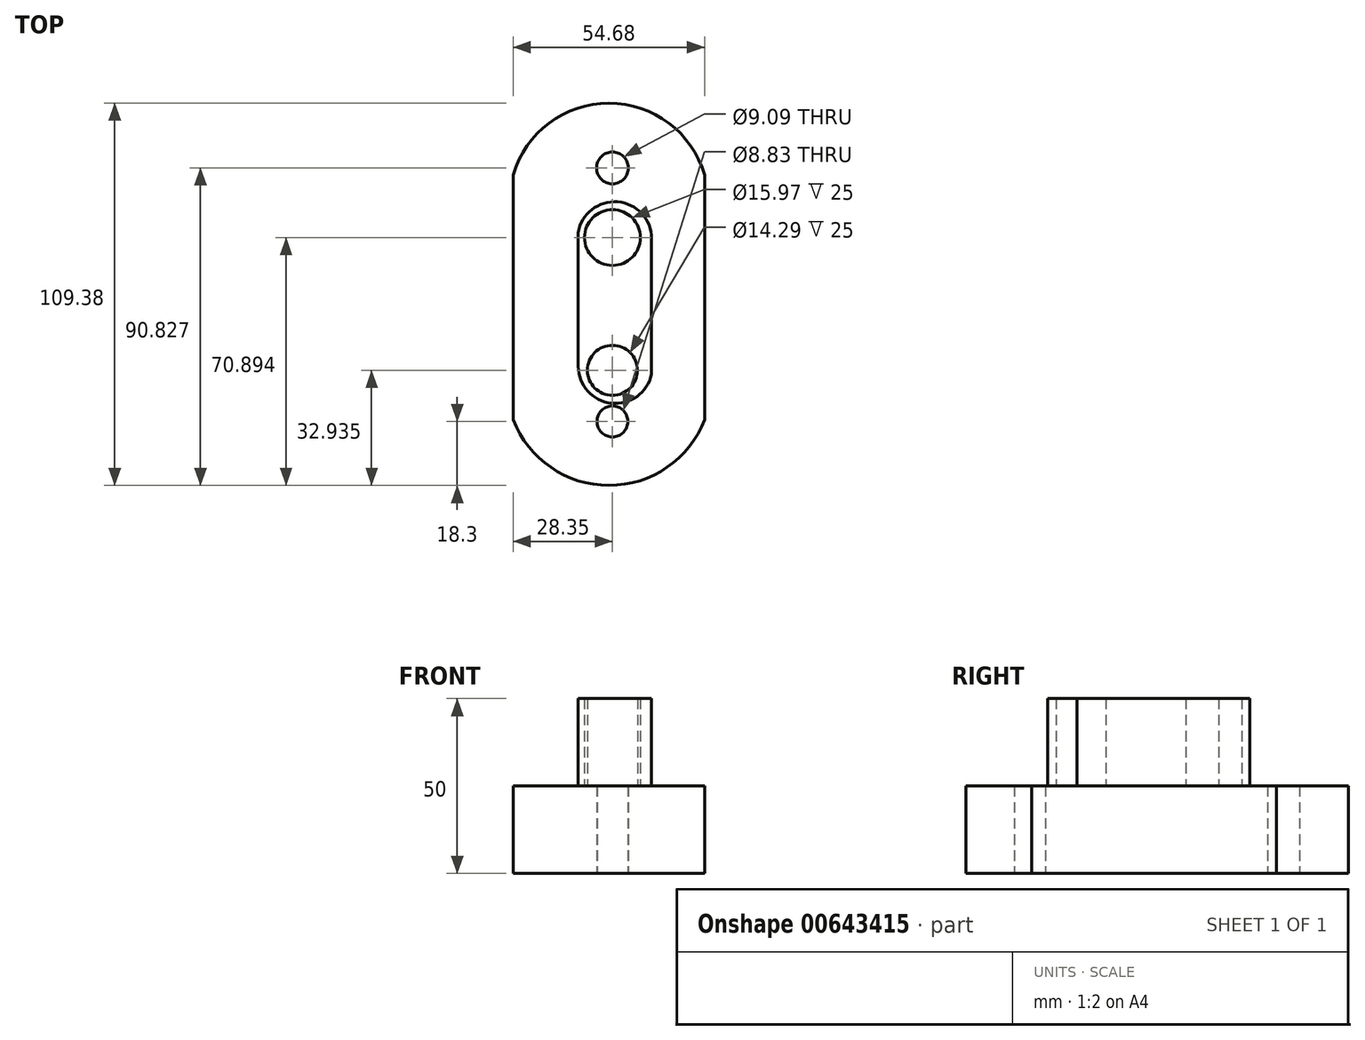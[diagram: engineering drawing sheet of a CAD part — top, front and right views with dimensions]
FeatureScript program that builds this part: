
annotation { "Feature Type Name" : "Feature", "Feature Type Description" : "" }
export const myFeature = defineFeature(function(context is Context, id is Id, definition is map)
    precondition{}
    {
        {
            var Q0;
            Q0=qCreatedBy(makeId("Top.planeOp"),FACE);
            var sketch = newSketch(context, id + "F0", { "sketchPlane" : qUnion([Q0])});
            skLineSegment(sketch, "E0", {"start": v(-28.35, 22.62) * mm, "end": v(-28.35, -47.38) * mm});
            skLineSegment(sketch, "E1", {"start": v(26.33, 22.62) * mm, "end": v(26.33, -47.38) * mm});
            skArc(sketch, "E2", {"start": v(26.33, 22.62) * mm, "mid": v(-1, 43.16) * mm, "end": v(-28.35, 22.62) * mm});
            skArc(sketch, "E3", {"start": v(-28.35, -47.38) * mm, "mid": v(-1, -66.22) * mm, "end": v(26.33, -47.38) * mm});
            skCircle(sketch, "E4", {"center": v(0, 24.6) * mm, "radius": 4.54 * mm});
            skCircle(sketch, "E5", {"center": v(0, -47.92) * mm, "radius": 4.41 * mm});
            skSolve(sketch);
        }
        {
            var Q0;
            Q0 = qSketchRegion(id + "F0", true);
            extrude(context, id + "F1", {"entities" : qUnion([Q0]), "depth" : 25 * mm, "offsetDistance" : 25 * mm});
        }
        {
            var Q0;
            Q0=makeQuery(id+"F1.opExtrude","CAP_FACE",FACE,{"disambiguationData":[OSD([sQuery(id+"F0.wireOp",EDGE,"E0"),sQuery(id+"F0.wireOp",EDGE,"E1"),sQuery(id+"F0.wireOp",EDGE,"E2"),sQuery(id+"F0.wireOp",EDGE,"E3"),sQuery(id+"F0.wireOp",EDGE,"E4"),sQuery(id+"F0.wireOp",EDGE,"E5")])],"isStart":false});
            var sketch = newSketch(context, id + "F2", { "sketchPlane" : qUnion([Q0])});
            skCircle(sketch, "E6", {"center": v(0, 4.67) * mm, "radius": 7.98 * mm});
            skCircle(sketch, "E7", {"center": v(0, -33.28) * mm, "radius": 7.15 * mm});
            skLineSegment(sketch, "E8", {"start": v(-9.77, -32.15) * mm, "end": v(-9.77, 6.1) * mm});
            skLineSegment(sketch, "E9", {"start": v(11.19, -34.42) * mm, "end": v(11.19, 4.4) * mm});
            skArc(sketch, "E10", {"start": v(11.19, 4.4) * mm, "mid": v(1.5, 14.9) * mm, "end": v(-9.77, 6.1) * mm});
            skArc(sketch, "E11", {"start": v(-9.77, -32.15) * mm, "mid": v(-0.3, -42.7) * mm, "end": v(11.19, -34.42) * mm});
            skSolve(sketch);
        }
        {
            var Q0;
            Q0 = qSketchRegion(id + "F2", true);
            extrude(context, id + "F3", {"entities" : qUnion([Q0]), "operationType" : NewBodyOperationType.ADD, "depth" : 25 * mm, "offsetDistance" : 25 * mm});
        }
    });
